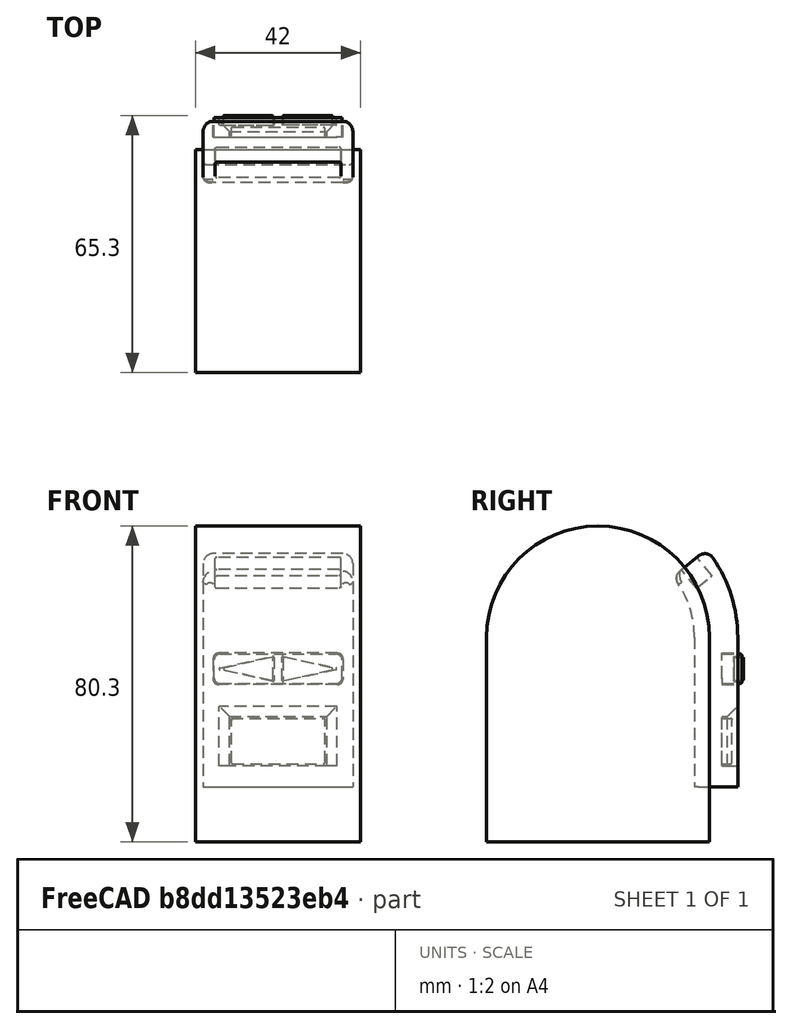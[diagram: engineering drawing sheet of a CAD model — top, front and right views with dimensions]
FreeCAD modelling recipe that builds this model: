
FCSTD DOCUMENT  (FreeCAD 0.20R29603 (Git))
Label: arm - pre-cutup
License: All rights reserved
LicenseURL: http://en.wikipedia.org/wiki/All_rights_reserved
objects: Part::Box×10, Part::Fillet×7, Part::MultiFuse×6, Part::Cut×6, Sketcher::SketchObject×4, PartDesign::Pad×4, PartDesign::Body×4, Part::Cylinder×3, Mesh::Feature×1, Spreadsheet::Sheet×1, Part::MultiCommon×1, Part::Wedge×1
note: 50 computed .brp shape members not serialized (recipe doc carries the construction recipe); baked Part::Feature solids carry a one-line shape summary decoded from their .brp

FEATURE [Mesh::Feature] Display_Arm
  Placement = pos=(0,13.65,-35) rot=(0,0,1;0rad)
FEATURE [Part::Cylinder] Cylinder  label="Underside cylinder"
  Angle = 360
  AttacherType = Attacher::AttachEngine3D
  FirstAngle = 0
  Height = 42
  Placement = pos=(-2,-6.5,0) rot=(0,-1,0;4.71239rad)
  Radius = 24.5
  SecondAngle = 0
  expr: .Placement.Base.y = -Spreadsheet.B1 + 18
  expr: Radius = Spreadsheet.B1
FEATURE [Spreadsheet::Sheet] Spreadsheet
  cells = A1=underside radius; B1=24.5; D1=triangle width; E1=5.9; G1=6.5; A2=topside radius; B2=40; D2=triangle height; E2=12.5; F2=1.04; G2=13.75; A3=Arm thickness; B3=11; D3=triangle filet; E3=0.25; G3==E3 * F2; A4=bisect radius; B4=28.3; D4=filet top; E4=0.25; G4==E4 * F2; A5=led channel cut; B5=31
FEATURE [Part::Box] Box  label="Cube"
  AttacherType = Attacher::AttachEngine3D
  Height = 52
  Length = 42
  Placement = pos=(-2,18,0) rot=(1,0,0;3.14159rad)
  Width = 49
  expr: Width = Spreadsheet.B1 * 2
FEATURE [Part::Cylinder] Cylinder001  label="top cylinder"
  Angle = 360
  AttacherType = Attacher::AttachEngine3D
  FirstAngle = 0
  Height = 42
  Placement = pos=(-2,-6.5,0) rot=(0,1,0;1.5708rad)
  Radius = 35.5
  SecondAngle = 0
  expr: .Placement.Base.y = -Spreadsheet.B1 + 18
  expr: Radius = Spreadsheet.B1 + Spreadsheet.B3
FEATURE [Part::Box] Box001  label="Cube001"
  AttacherType = Attacher::AttachEngine3D
  Height = 52
  Length = 42
  Placement = pos=(-2,29,0) rot=(1,0,0;3.14159rad)
  Width = 71
  expr: .Placement.Base.y = 18 + Spreadsheet.B3
  expr: Width = (Spreadsheet.B1 + Spreadsheet.B3) * 2
FEATURE [Part::MultiFuse] Fusion  label="Underside cut"
  Shapes = -> [Cylinder,Box]
FEATURE [Part::MultiFuse] Fusion001  label="Topside intersect"
  Shapes = -> [Cylinder001,Box001]
FEATURE [Part::Box] Box002  label="Cube002"
  AttacherType = Attacher::AttachEngine3D
  Height = 76
  Length = 38
  Placement = pos=(0,10,-38) rot=(0,0,1;0rad)
  Width = 20
FEATURE [Part::Cut] Cut
  Base = -> Box002
  Tool = -> Fusion
FEATURE [Part::MultiCommon] Common
  Shapes = -> [Cut,Fusion001]
FEATURE [Part::Box] Box003  label="Cube003"
  AttacherType = Attacher::AttachEngine3D
  Height = 27
  Length = 56
  Placement = pos=(-5,-6.5,0) rot=(-1,0,0;5.60251rad)
  Width = 48
FEATURE [Part::Cut] Cut001
  Base = -> Common
  Tool = -> Box003
FEATURE [Part::Fillet] Fillet
  Base = -> Cut001
  Edges = 12 edges: [Edge1 r=2.5,Edge2 r=2.5,Edge3 r=2.5,Edge5 r=1,Edge6 r=1,Edge7 r=2.5,Edge8 r=2.5,Edge9 r=2.5,Edge10 r=2.5,Edge12 r=2.5,Edge17 r=1,Edge18 r=1]
FEATURE [Sketcher::SketchObject] Sketch
  FullyConstrained = true
  MapMode = 5
  Placement = pos=(0,0,0) rot=(1,0,0;1.5708rad)
  Support = -> [XZ_Plane]
  expr: .Constraints.Base filet = Spreadsheet.E3
  expr: .Constraints.Base filet 2 = Spreadsheet.E3
  expr: .Constraints.base = Spreadsheet.E1
  expr: .Constraints.filet top = Spreadsheet.E4
  expr: Constraints[6] = (Spreadsheet.E1 * Spreadsheet.E1 + Spreadsheet.E2 * Spreadsheet.E2) ^ (1 / 2)
  expr: Constraints[7] = (Spreadsheet.E1 * Spreadsheet.E1 + Spreadsheet.E2 * Spreadsheet.E2) ^ (1 / 2)
  sketch-geometry (10):
    g0: LineSegment StartX=-0.24424 StartY=5.95617 StartZ=0 EndX=-2.88373 EndY=-6.12642 EndZ=0
    g1: LineSegment StartX=-2.63949 StartY=-6.42977 StartZ=0 EndX=2.63949 EndY=-6.42977 EndZ=0
    g2: LineSegment StartX=2.88373 StartY=-6.12642 StartZ=0 EndX=0.24424 EndY=5.95617 EndZ=0
    g3: Circle CenterX=0 CenterY=0 CenterZ=0 NormalX=0 NormalY=0 NormalZ=1 AngleXU=0 Radius=7.07421
    g4: ArcOfCircle CenterX=1.3e-15 CenterY=5.90282 CenterZ=0 NormalX=0 NormalY=0 NormalZ=1 AngleXU=0 Radius=0.25 StartAngle=0.215075 EndAngle=2.92652
    g5: GeomPoint X=1.5e-15 Y=7.07421 Z=0
    g6: ArcOfCircle CenterX=-2.63949 CenterY=-6.17977 CenterZ=0 NormalX=0 NormalY=0 NormalZ=1 AngleXU=0 Radius=0.25 StartAngle=2.92652 EndAngle=4.71239
    g7: GeomPoint X=-2.95 Y=-6.42977 Z=0
    g8: ArcOfCircle CenterX=2.63949 CenterY=-6.17977 CenterZ=0 NormalX=0 NormalY=0 NormalZ=1 AngleXU=0 Radius=0.25 StartAngle=4.71239 EndAngle=6.49826
    g9: GeomPoint X=2.95 Y=-6.42977 Z=0
  constraints (23):
    c: PointOnObject(g7,g3)
    c: PointOnObject(g9,g3)
    c: PointOnObject(g5,g3)
    c: Coincident(g3,g-1)
    c: Horizontal(g1)
    c: Distance(g9,g7) = 5.9  'base'
    c: Distance(g9,g5) = 13.8224
    c: Distance(g7,g5) = 13.8224
    c: PointOnObject(g5,g0)
    c: PointOnObject(g5,g2)
    c: Tangent(g0,g4) = -1.5708
    c: Tangent(g2,g4) = -1.5708
    c: Radius(g4) = 0.25  'filet top'
    c: PointOnObject(g7,g0)
    c: PointOnObject(g7,g1)
    c: Tangent(g0,g6) = -1.5708
    c: Tangent(g1,g6) = -1.5708
    c: PointOnObject(g9,g1)
    c: PointOnObject(g9,g2)
    c: Tangent(g1,g8) = -1.5708
    c: Tangent(g2,g8) = -1.5708
    c: Radius(g8) = 0.25  'Base filet'
    c: Radius(g6) = 0.25  'Base filet 2'
FEATURE [PartDesign::Pad] Pad
  Direction = (0,-1,2e-16)
  Length = 2.5
  Length2 = 10
  Placement = pos=(0,0,0) rot=(1,0,0;1.5708rad)
  Profile = -> Sketch
  ReferenceAxis = -> Sketch [N_Axis]
  Type = 0
FEATURE [PartDesign::Body] Body
  Group = -> [Sketch,Pad]
  Origin = -> Origin
  Placement = pos=(26.7,63,-8) rot=(0,1,0;1.5708rad)
  Tip = -> Pad
FEATURE [Sketcher::SketchObject] Sketch001
  FullyConstrained = true
  MapMode = 5
  Placement = pos=(0,0,0) rot=(1,0,0;1.5708rad)
  Support = -> [XZ_Plane]
  expr: .Constraints.Base filet = Spreadsheet.G3
  expr: .Constraints.Base filet 2 = Spreadsheet.G3
  expr: .Constraints.base = Spreadsheet.G1
  expr: .Constraints.filet top = Spreadsheet.G4
  expr: .Constraints.hyp 1 = (Spreadsheet.G1 ^ 2 + Spreadsheet.G2 ^ 2) ^ (1 / 2)
  expr: .Constraints.hyp 2 = (Spreadsheet.G1 ^ 2 + Spreadsheet.G2 ^ 2) ^ (1 / 2)
  sketch-geometry (10):
    g0: LineSegment StartX=-0.253994 StartY=6.62313 StartZ=0 EndX=-3.18097 EndY=-6.75781 EndZ=0
    g1: LineSegment StartX=-2.92698 StartY=-7.07337 StartZ=0 EndX=2.92698 EndY=-7.07337 EndZ=0
    g2: LineSegment StartX=3.18097 StartY=-6.75781 StartZ=0 EndX=0.253994 EndY=6.62313 EndZ=0
    g3: Circle CenterX=0 CenterY=0 CenterZ=0 NormalX=0 NormalY=0 NormalZ=1 AngleXU=0 Radius=7.78429
    g4: ArcOfCircle CenterX=-1e-15 CenterY=6.56757 CenterZ=0 NormalX=0 NormalY=0 NormalZ=1 AngleXU=0 Radius=0.26 StartAngle=0.21535 EndAngle=2.92624
    g5: GeomPoint X=-1.1e-15 Y=7.78429 Z=0
    g6: ArcOfCircle CenterX=-2.92698 CenterY=-6.81337 CenterZ=0 NormalX=0 NormalY=0 NormalZ=1 AngleXU=0 Radius=0.26 StartAngle=2.92624 EndAngle=4.71239
    g7: GeomPoint X=-3.25 Y=-7.07337 Z=0
    g8: ArcOfCircle CenterX=2.92698 CenterY=-6.81337 CenterZ=0 NormalX=0 NormalY=0 NormalZ=1 AngleXU=0 Radius=0.26 StartAngle=4.71239 EndAngle=6.49854
    g9: GeomPoint X=3.25 Y=-7.07337 Z=0
  constraints (23):
    c: PointOnObject(g7,g3)
    c: PointOnObject(g9,g3)
    c: PointOnObject(g5,g3)
    c: Coincident(g3,g-1)
    c: Horizontal(g1)
    c: Distance(g9,g7) = 6.5  'base'
    c: Distance(g9,g5) = 15.209  'hyp 1'
    c: Distance(g7,g5) = 15.209  'hyp 2'
    c: PointOnObject(g5,g0)
    c: PointOnObject(g5,g2)
    c: Tangent(g0,g4) = -1.5708
    c: Tangent(g2,g4) = -1.5708
    c: Radius(g4) = 0.26  'filet top'
    c: PointOnObject(g7,g0)
    c: PointOnObject(g7,g1)
    c: Tangent(g0,g6) = -1.5708
    c: Tangent(g1,g6) = -1.5708
    c: PointOnObject(g9,g1)
    c: PointOnObject(g9,g2)
    c: Tangent(g1,g8) = -1.5708
    c: Tangent(g2,g8) = -1.5708
    c: Radius(g8) = 0.26  'Base filet'
    c: Radius(g6) = 0.26  'Base filet 2'
FEATURE [PartDesign::Pad] Pad001
  Direction = (0,-1,2e-16)
  Length = 10
  Length2 = 10
  Placement = pos=(0,0,0) rot=(1,0,0;1.5708rad)
  Profile = -> Sketch001
  ReferenceAxis = -> Sketch001 [N_Axis]
  Type = 0
FEATURE [PartDesign::Body] Body001
  Group = -> [Sketch001,Pad001]
  Origin = -> Origin001
  Placement = pos=(27.1,63,-8) rot=(0,1,0;1.5708rad)
  Tip = -> Pad001
FEATURE [Sketcher::SketchObject] Sketch002
  FullyConstrained = true
  MapMode = 5
  Placement = pos=(0,0,0) rot=(1,0,0;1.5708rad)
  Support = -> [XZ_Plane]
  sketch-geometry (10):
    g0: LineSegment StartX=-0.24424 StartY=5.95617 StartZ=0 EndX=-2.88373 EndY=-6.12642 EndZ=0
    g1: LineSegment StartX=-2.63949 StartY=-6.42977 StartZ=0 EndX=2.63949 EndY=-6.42977 EndZ=0
    g2: LineSegment StartX=2.88373 StartY=-6.12642 StartZ=0 EndX=0.24424 EndY=5.95617 EndZ=0
    g3: Circle CenterX=0 CenterY=0 CenterZ=0 NormalX=0 NormalY=0 NormalZ=1 AngleXU=0 Radius=7.07421
    g4: ArcOfCircle CenterX=1.3e-15 CenterY=5.90282 CenterZ=0 NormalX=0 NormalY=0 NormalZ=1 AngleXU=0 Radius=0.25 StartAngle=0.215075 EndAngle=2.92652
    g5: GeomPoint X=1.5e-15 Y=7.07421 Z=0
    g6: ArcOfCircle CenterX=-2.63949 CenterY=-6.17977 CenterZ=0 NormalX=0 NormalY=0 NormalZ=1 AngleXU=0 Radius=0.25 StartAngle=2.92652 EndAngle=4.71239
    g7: GeomPoint X=-2.95 Y=-6.42977 Z=0
    g8: ArcOfCircle CenterX=2.63949 CenterY=-6.17977 CenterZ=0 NormalX=0 NormalY=0 NormalZ=1 AngleXU=0 Radius=0.25 StartAngle=4.71239 EndAngle=6.49826
    g9: GeomPoint X=2.95 Y=-6.42977 Z=0
  constraints (23):
    c: PointOnObject(g7,g3)
    c: PointOnObject(g9,g3)
    c: PointOnObject(g5,g3)
    c: Coincident(g3,g-1)
    c: Horizontal(g1)
    c: Distance(g9,g7) = 5.9  'base'
    c: Distance(g9,g5) = 13.8224
    c: Distance(g7,g5) = 13.8224
    c: PointOnObject(g5,g0)
    c: PointOnObject(g5,g2)
    c: Tangent(g0,g4) = -1.5708
    c: Tangent(g2,g4) = -1.5708
    c: Radius(g4) = 0.25  'filet top'
    c: PointOnObject(g7,g0)
    c: PointOnObject(g7,g1)
    c: Tangent(g0,g6) = -1.5708
    c: Tangent(g1,g6) = -1.5708
    c: PointOnObject(g9,g1)
    c: PointOnObject(g9,g2)
    c: Tangent(g1,g8) = -1.5708
    c: Tangent(g2,g8) = -1.5708
    c: Radius(g8) = 0.25  'Base filet'
    c: Radius(g6) = 0.25  'Base filet 2'
FEATURE [PartDesign::Pad] Pad002
  Direction = (0,-1,2e-16)
  Length = 2.5
  Length2 = 10
  Placement = pos=(0,0,0) rot=(1,0,0;1.5708rad)
  Profile = -> Sketch002
  ReferenceAxis = -> Sketch002 [N_Axis]
  Type = 0
FEATURE [PartDesign::Body] Body002
  Group = -> [Sketch002,Pad002]
  Origin = -> Origin002
  Placement = pos=(11.3,63,-8) rot=(0,-1,0;1.5708rad)
  Tip = -> Pad002
FEATURE [Sketcher::SketchObject] Sketch003
  FullyConstrained = true
  MapMode = 5
  Placement = pos=(0,0,0) rot=(1,0,0;1.5708rad)
  Support = -> [XZ_Plane]
  sketch-geometry (10):
    g0: LineSegment StartX=-0.253994 StartY=6.62313 StartZ=0 EndX=-3.18097 EndY=-6.75781 EndZ=0
    g1: LineSegment StartX=-2.92698 StartY=-7.07337 StartZ=0 EndX=2.92698 EndY=-7.07337 EndZ=0
    g2: LineSegment StartX=3.18097 StartY=-6.75781 StartZ=0 EndX=0.253994 EndY=6.62313 EndZ=0
    g3: Circle CenterX=0 CenterY=0 CenterZ=0 NormalX=0 NormalY=0 NormalZ=1 AngleXU=0 Radius=7.78429
    g4: ArcOfCircle CenterX=-1e-15 CenterY=6.56757 CenterZ=0 NormalX=0 NormalY=0 NormalZ=1 AngleXU=0 Radius=0.26 StartAngle=0.21535 EndAngle=2.92624
    g5: GeomPoint X=-1.1e-15 Y=7.78429 Z=0
    g6: ArcOfCircle CenterX=-2.92698 CenterY=-6.81337 CenterZ=0 NormalX=0 NormalY=0 NormalZ=1 AngleXU=0 Radius=0.26 StartAngle=2.92624 EndAngle=4.71239
    g7: GeomPoint X=-3.25 Y=-7.07337 Z=0
    g8: ArcOfCircle CenterX=2.92698 CenterY=-6.81337 CenterZ=0 NormalX=0 NormalY=0 NormalZ=1 AngleXU=0 Radius=0.26 StartAngle=4.71239 EndAngle=6.49854
    g9: GeomPoint X=3.25 Y=-7.07337 Z=0
  constraints (23):
    c: PointOnObject(g7,g3)
    c: PointOnObject(g9,g3)
    c: PointOnObject(g5,g3)
    c: Coincident(g3,g-1)
    c: Horizontal(g1)
    c: Distance(g9,g7) = 6.5  'base'
    c: Distance(g9,g5) = 15.209  'hyp 1'
    c: Distance(g7,g5) = 15.209  'hyp 2'
    c: PointOnObject(g5,g0)
    c: PointOnObject(g5,g2)
    c: Tangent(g0,g4) = -1.5708
    c: Tangent(g2,g4) = -1.5708
    c: Radius(g4) = 0.26  'filet top'
    c: PointOnObject(g7,g0)
    c: PointOnObject(g7,g1)
    c: Tangent(g0,g6) = -1.5708
    c: Tangent(g1,g6) = -1.5708
    c: PointOnObject(g9,g1)
    c: PointOnObject(g9,g2)
    c: Tangent(g1,g8) = -1.5708
    c: Tangent(g2,g8) = -1.5708
    c: Radius(g8) = 0.26  'Base filet'
    c: Radius(g6) = 0.26  'Base filet 2'
FEATURE [PartDesign::Pad] Pad003
  Direction = (0,-1,2e-16)
  Length = 10
  Length2 = 10
  Placement = pos=(0,0,0) rot=(1,0,0;1.5708rad)
  Profile = -> Sketch003
  ReferenceAxis = -> Sketch003 [N_Axis]
  Type = 0
FEATURE [PartDesign::Body] Body003
  Group = -> [Sketch003,Pad003]
  Origin = -> Origin003
  Placement = pos=(10.9,63,-8) rot=(0,1,0;4.71239rad)
  Tip = -> Pad003
FEATURE [Part::Box] Box005  label="Cube005"
  AttacherType = Attacher::AttachEngine3D
  Height = 7.5
  Length = 32.52
  Placement = pos=(2.75,25,-11.75) rot=(0,0,1;0rad)
  Width = 5
FEATURE [Part::Box] Box006  label="Cube006"
  AttacherType = Attacher::AttachEngine3D
  Height = 8
  Length = 33.02
  Placement = pos=(2.5,25,-12) rot=(0,0,1;0rad)
  Width = 5
FEATURE [Part::Fillet] Fillet001
  Base = -> Box006
  Edges = 4 edges r=1.5: [Edge2,Edge4,Edge6,Edge8]
FEATURE [Part::Cut] Cut002
  Base = -> Fillet
  Tool = -> Fillet001
FEATURE [Part::Fillet] Fillet002
  Base = -> Box005
  Edges = 4 edges r=1.5: [Edge2,Edge4,Edge6,Edge8]
FEATURE [Part::MultiFuse] Fusion003  label="wedge holes"
  Placement = pos=(0,-25,0) rot=(0,0,1;0rad)
  Shapes = -> [Body003,Body001]
FEATURE [Part::Cut] Cut003  label="panel"
  Base = -> Fillet002
  Tool = -> Fusion003
FEATURE [Part::MultiFuse] Fusion004  label="Arrows"
  Placement = pos=(0,-32.5,0) rot=(0,0,1;0rad)
  Shapes = -> [Body002,Body]
FEATURE [Part::Wedge] Wedge
  AttacherType = Attacher::AttachEngine3D
  Placement = pos=(6.65,26.4,-24.1) rot=(0,0,1;0rad)
  X2max = 30.75
  X2min = -6
  Xmax = 24.75
  Xmin = 0
  Ymax = 6
  Ymin = 0
  Z2max = 10
  Z2min = -8.5
  Zmax = 4
  Zmin = -8.5
FEATURE [Part::Box] Box007  label="Cube007"
  AttacherType = Attacher::AttachEngine3D
  Height = 12.5
  Length = 24.75
  Placement = pos=(6.65,25,-32.6) rot=(0,0,1;0rad)
  Width = 5
FEATURE [Part::Box] Box008  label="Cube008"
  AttacherType = Attacher::AttachEngine3D
  Height = 11.5
  Length = 23.75
  Placement = pos=(7.15,25,-32.1) rot=(0,0,1;0rad)
  Width = 2.5
FEATURE [Part::MultiFuse] Fusion005
  Shapes = -> [Box007,Wedge]
FEATURE [Part::Cut] Cut004
  Base = -> Cut002
  Tool = -> Fusion005
FEATURE [Part::Fillet] Fillet003
  Base = -> Cut003
  Edges = 20 edges r=0.25: [Edge3,Edge13,Edge14,Edge15,Edge16,Edge17,Edge18,Edge19,Edge20,Edge21,Edge22,Edge23,Edge24,Edge25,Edge26,Edge27,Edge28,Edge29,Edge30,Edge31]
FEATURE [Part::Fillet] Fillet004
  Base = -> Fusion004
  Edges = 12 edges r=0.25: [Edge3,Edge6,Edge9,Edge12,Edge15,Edge17,Edge21,Edge24,Edge27,Edge30,Edge33,Edge35]
FEATURE [Part::Fillet] Fillet005
  Base = -> Box008
  Edges = 7 edges r=0.25: [Edge3,Edge4,Edge6,Edge7,Edge8,Edge11,Edge12]
FEATURE [Part::Box] Box009  label="Cube009"
  AttacherType = Attacher::AttachEngine3D
  Height = 27
  Length = 32
  Placement = pos=(3.02,18.5342,12.5131) rot=(1,0,0;0.680678rad)
  Width = 5.02
FEATURE [Part::Fillet] Fillet006
  Base = -> Box009
  Edges = 4 edges r=0.5: [Edge1,Edge3,Edge5,Edge7]
FEATURE [Part::Cut] Cut005
  Base = -> Cut004
  Tool = -> Fillet006
FEATURE [Part::Box] Box004  label="Cube004"
  AttacherType = Attacher::AttachEngine3D
  Height = 52
  Length = 42
  Placement = pos=(-2,21.8,0) rot=(1,0,0;3.14159rad)
  Width = 56.6
  expr: .Placement.Base.y = 18 + Spreadsheet.B4 - Spreadsheet.B1
  expr: Width = Spreadsheet.B4 * 2
FEATURE [Part::Cylinder] Cylinder002  label="top cylinder001"
  Angle = 360
  AttacherType = Attacher::AttachEngine3D
  FirstAngle = 0
  Height = 42
  Placement = pos=(-2,-6.5,0) rot=(0,1,0;1.5708rad)
  Radius = 28.3
  SecondAngle = 0
  expr: .Placement.Base.y = -Spreadsheet.B1 + 18
  expr: Radius = Spreadsheet.B4
FEATURE [Part::MultiFuse] Fusion002  label="Bisect intersect"
  Shapes = -> [Box004,Cylinder002]
